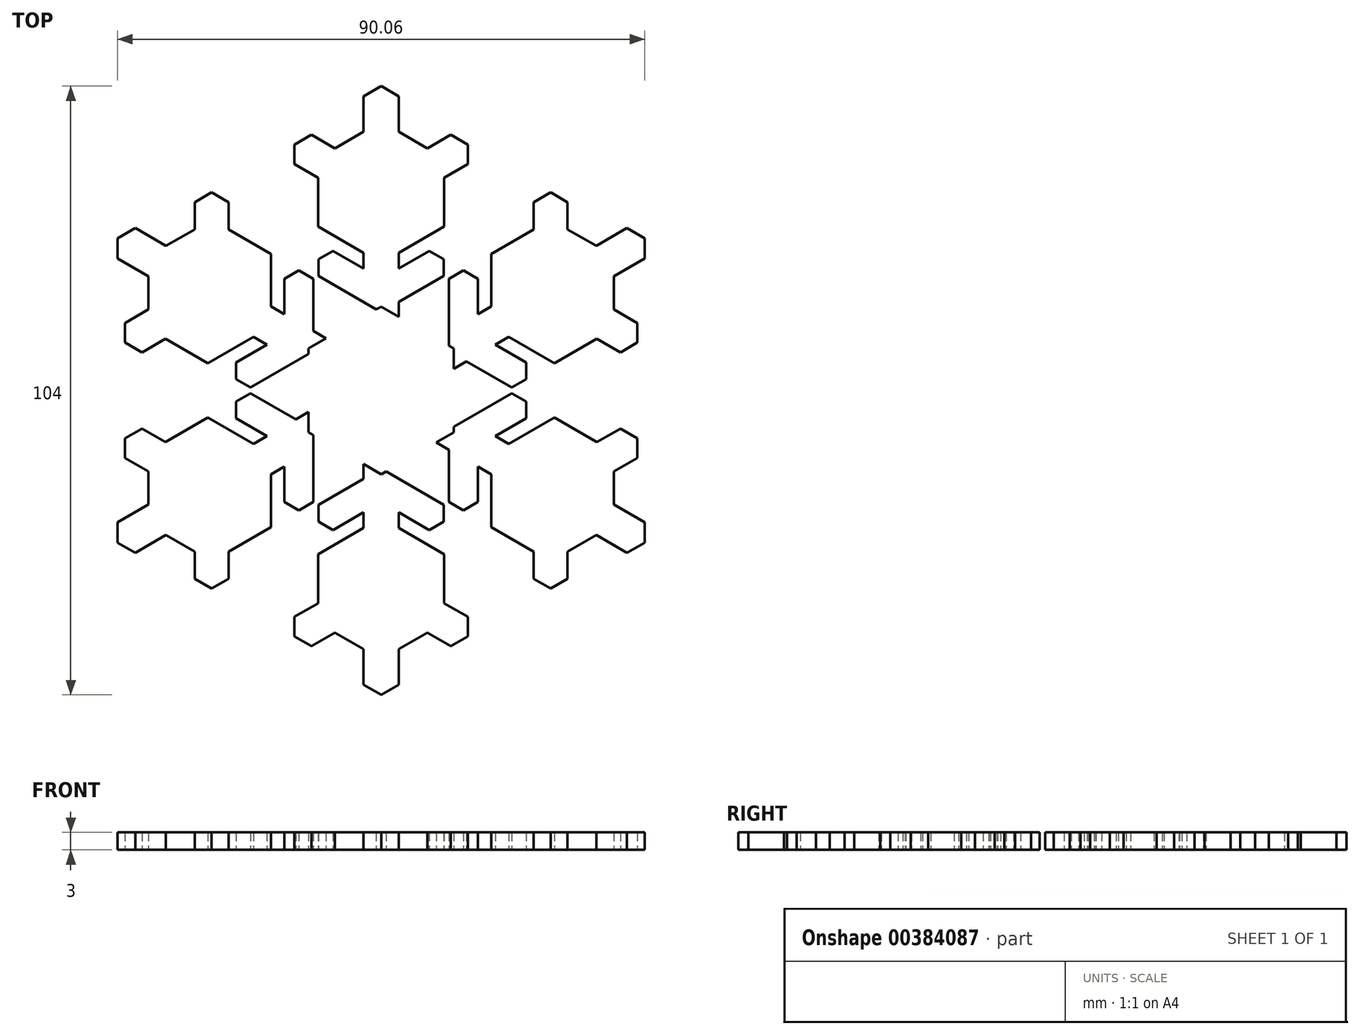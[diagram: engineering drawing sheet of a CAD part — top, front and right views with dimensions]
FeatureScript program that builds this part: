
annotation { "Feature Type Name" : "Feature", "Feature Type Description" : "" }
export const myFeature = defineFeature(function(context is Context, id is Id, definition is map)
    precondition{}
    {
        {
            var Q0;
            Q0=qCreatedBy(makeId("Top.planeOp"),FACE);
            var sketch = newSketch(context, id + "F0", { "sketchPlane" : qUnion([Q0])});
            skLineSegment(sketch, "E0", {"start": v(0, 26) * mm, "end": v(0, -26) * mm, "construction": true});
            skLineSegment(sketch, "E1", {"start": v(-22.52, -13) * mm, "end": v(22.52, 13) * mm, "construction": true});
            skLineSegment(sketch, "E2", {"start": v(22.52, -13) * mm, "end": v(-22.52, 13) * mm, "construction": true});
            skLineSegment(sketch, "E3", {"start": v(0, 7.16) * mm, "end": v(-6.2, 3.58) * mm});
            skLineSegment(sketch, "E4", {"start": v(-3.2, 1.85) * mm, "end": v(0, 3.7) * mm});
            skLineSegment(sketch, "E5", {"start": v(-1.5, 6.3) * mm, "end": v(-1.5, 11.75) * mm});
            skLineSegment(sketch, "E6", {"start": v(-1.5, 11.75) * mm, "end": v(-5.4, 14) * mm});
            skLineSegment(sketch, "E7", {"start": v(-5.4, 14) * mm, "end": v(-5.4, 19.85) * mm});
            skLineSegment(sketch, "E8", {"start": v(-5.4, 19.85) * mm, "end": v(-1.5, 22.1) * mm});
            skLineSegment(sketch, "E9", {"start": v(-1.5, 22.1) * mm, "end": v(-1.5, 25.13) * mm});
            skLineSegment(sketch, "E10", {"start": v(-1.5, 25.13) * mm, "end": v(0, 26) * mm});
            skLineSegment(sketch, "E11", {"start": v(-5.4, 18.18) * mm, "end": v(-7.4, 19.34) * mm});
            skLineSegment(sketch, "E12", {"start": v(-7.4, 19.34) * mm, "end": v(-7.4, 21) * mm});
            skLineSegment(sketch, "E13", {"start": v(-7.4, 21) * mm, "end": v(-5.95, 21.84) * mm});
            skLineSegment(sketch, "E14", {"start": v(-5.95, 21.84) * mm, "end": v(-3.95, 20.68) * mm});
            skLineSegment(sketch, "E15", {"start": v(-1.5, 22.1) * mm, "end": v(-1.5, 11.75) * mm, "construction": true});
            skLineSegment(sketch, "E16", {"start": v(-7.4, 19.34) * mm, "end": v(-5.95, 21.84) * mm, "construction": true});
            skLineSegment(sketch, "E17", {"start": v(-7.4, 21) * mm, "end": v(-6.68, 20.59) * mm, "construction": true});
            skLineSegment(sketch, "E18", {"start": v(-6.68, 20.59) * mm, "end": v(-5.4, 19.85) * mm, "construction": true});
            skLineSegment(sketch, "E19", {"start": v(-1.5, 10.4) * mm, "end": v(-4.12, 11.92) * mm});
            skLineSegment(sketch, "E20", {"start": v(-4.12, 11.92) * mm, "end": v(-5.36, 11.2) * mm});
            skLineSegment(sketch, "E21", {"start": v(-5.36, 11.2) * mm, "end": v(-5.36, 9.78) * mm});
            skLineSegment(sketch, "E22", {"start": v(-5.36, 9.78) * mm, "end": v(-0.42, 6.92) * mm});
            skLineSegment(sketch, "E23", {"start": v(-5.36, 9.78) * mm, "end": v(-4.12, 11.92) * mm, "construction": true});
            skPoint(sketch, "E24.endSnap0", {"position": v(-4.74, 10.85) * mm});
            skLineSegment(sketch, "E25", {"start": v(-5.36, 11.2) * mm, "end": v(-4.74, 10.85) * mm, "construction": true});
            skLineSegment(sketch, "E26.MirrorCS", {"start": v(7.4, 19.34) * mm, "end": v(5.95, 21.84) * mm, "construction": true});
            skLineSegment(sketch, "E27.MirrorCS", {"start": v(7.4, 19.34) * mm, "end": v(7.4, 21) * mm});
            skLineSegment(sketch, "E28.MirrorCS", {"start": v(6.68, 20.59) * mm, "end": v(5.4, 19.85) * mm, "construction": true});
            skLineSegment(sketch, "E29.MirrorCS", {"start": v(7.4, 21) * mm, "end": v(5.95, 21.84) * mm});
            skLineSegment(sketch, "E30.MirrorCS", {"start": v(7.4, 21) * mm, "end": v(6.68, 20.59) * mm, "construction": true});
            skLineSegment(sketch, "E31.MirrorCS", {"start": v(1.5, 25.13) * mm, "end": v(0, 26) * mm});
            skLineSegment(sketch, "E32.MirrorCS", {"start": v(5.36, 11.2) * mm, "end": v(4.74, 10.85) * mm, "construction": true});
            skLineSegment(sketch, "E33.MirrorCS", {"start": v(1.5, 22.1) * mm, "end": v(1.5, 25.13) * mm});
            skLineSegment(sketch, "E34.MirrorCS", {"start": v(5.4, 19.85) * mm, "end": v(1.5, 22.1) * mm});
            skLineSegment(sketch, "E35.MirrorCS", {"start": v(1.5, 10.4) * mm, "end": v(4.12, 11.92) * mm});
            skLineSegment(sketch, "E36.MirrorCS", {"start": v(4.12, 11.92) * mm, "end": v(5.36, 11.2) * mm});
            skLineSegment(sketch, "E37.MirrorCS", {"start": v(5.36, 9.78) * mm, "end": v(0.42, 6.92) * mm});
            skLineSegment(sketch, "E38.MirrorCS", {"start": v(5.36, 9.78) * mm, "end": v(4.12, 11.92) * mm, "construction": true});
            skLineSegment(sketch, "E39.MirrorCS", {"start": v(5.4, 18.18) * mm, "end": v(7.4, 19.34) * mm});
            skPoint(sketch, "E40.MirrorP", {"position": v(4.74, 10.85) * mm});
            skLineSegment(sketch, "E41.MirrorCS", {"start": v(3.2, 1.85) * mm, "end": v(0, 3.7) * mm});
            skLineSegment(sketch, "E42.MirrorCS", {"start": v(0, 7.16) * mm, "end": v(6.2, 3.58) * mm});
            skLineSegment(sketch, "E43.MirrorCS", {"start": v(1.5, 6.3) * mm, "end": v(1.5, 11.75) * mm});
            skLineSegment(sketch, "E44.MirrorCS", {"start": v(1.5, 11.75) * mm, "end": v(5.4, 14) * mm});
            skLineSegment(sketch, "E45.MirrorCS", {"start": v(5.36, 11.2) * mm, "end": v(5.36, 9.78) * mm});
            skLineSegment(sketch, "E46.MirrorCS", {"start": v(5.4, 14) * mm, "end": v(5.4, 19.85) * mm});
            skLineSegment(sketch, "E47.MirrorCS", {"start": v(1.5, 22.1) * mm, "end": v(1.5, 11.75) * mm, "construction": true});
            skLineSegment(sketch, "E48.MirrorCS", {"start": v(5.95, 21.84) * mm, "end": v(3.95, 20.68) * mm});
            skLineSegment(sketch, "E49.1.0", {"start": v(-8.26, 9.53) * mm, "end": v(-7.02, 10.25) * mm});
            skLineSegment(sketch, "E49.1.1", {"start": v(-12.39, 2.39) * mm, "end": v(-12.39, 0.96) * mm});
            skLineSegment(sketch, "E49.1.2", {"start": v(0, 3.7) * mm, "end": v(-3.2, 1.85) * mm});
            skLineSegment(sketch, "E49.1.3", {"start": v(-10.92, 4.57) * mm, "end": v(-14.82, 2.33) * mm});
            skLineSegment(sketch, "E49.1.4", {"start": v(-18.39, 12.35) * mm, "end": v(-9.42, 7.17) * mm, "construction": true});
            skLineSegment(sketch, "E49.1.5", {"start": v(-11.15, 0.24) * mm, "end": v(-12.39, 2.39) * mm, "construction": true});
            skLineSegment(sketch, "E49.1.6", {"start": v(-5.79, 9.53) * mm, "end": v(-5.79, 3.82) * mm});
            skLineSegment(sketch, "E49.1.7", {"start": v(-21.9, 5.76) * mm, "end": v(-19.89, 6.92) * mm});
            skLineSegment(sketch, "E49.1.8", {"start": v(-19.89, 9.75) * mm, "end": v(-10.92, 4.57) * mm, "construction": true});
            skLineSegment(sketch, "E49.1.9", {"start": v(-18.44, 4.42) * mm, "end": v(-20.45, 3.26) * mm});
            skLineSegment(sketch, "E49.1.10", {"start": v(-7.02, 10.25) * mm, "end": v(-5.79, 9.53) * mm});
            skLineSegment(sketch, "E49.1.11", {"start": v(-14.82, 2.33) * mm, "end": v(-19.89, 5.25) * mm});
            skLineSegment(sketch, "E49.1.12", {"start": v(-6.2, 1.85) * mm, "end": v(-10.92, 4.57) * mm});
            skLineSegment(sketch, "E49.1.13", {"start": v(-9.42, 7.17) * mm, "end": v(-9.42, 11.67) * mm});
            skLineSegment(sketch, "E49.1.14", {"start": v(-3.2, -1.85) * mm, "end": v(-3.2, 1.85) * mm});
            skLineSegment(sketch, "E49.1.15", {"start": v(-6.2, 3.58) * mm, "end": v(-6.2, -3.58) * mm});
            skLineSegment(sketch, "E49.1.16", {"start": v(-18.39, 12.35) * mm, "end": v(-21.02, 13.87) * mm});
            skPoint(sketch, "E49.1.17", {"position": v(-11.77, 1.32) * mm});
            skLineSegment(sketch, "E49.1.18", {"start": v(-9.42, 11.67) * mm, "end": v(-14.5, 14.6) * mm});
            skLineSegment(sketch, "E49.1.19", {"start": v(-6.2, 3.58) * mm, "end": v(0, 7.16) * mm});
            skLineSegment(sketch, "E49.1.20", {"start": v(-12.39, 0.96) * mm, "end": v(-11.15, 0.24) * mm});
            skLineSegment(sketch, "E49.1.21", {"start": v(-15.94, 16.08) * mm, "end": v(-15.94, 13.76) * mm});
            skLineSegment(sketch, "E49.1.22", {"start": v(-21.02, 13.87) * mm, "end": v(-22.52, 13) * mm});
            skLineSegment(sketch, "E49.1.23", {"start": v(-5.79, 9.53) * mm, "end": v(-8.26, 9.53) * mm, "construction": true});
            skPoint(sketch, "E49.1.24", {"position": v(-7.02, 9.53) * mm});
            skLineSegment(sketch, "E49.1.25", {"start": v(-4.7, 4.45) * mm, "end": v(-9.42, 7.17) * mm});
            skLineSegment(sketch, "E49.1.26", {"start": v(-11.15, 0.24) * mm, "end": v(-6.2, 3.1) * mm});
            skLineSegment(sketch, "E49.1.27", {"start": v(-13.05, 13.76) * mm, "end": v(-13.05, 16.08) * mm});
            skLineSegment(sketch, "E49.1.28", {"start": v(-8.26, 6.5) * mm, "end": v(-8.26, 9.53) * mm});
            skLineSegment(sketch, "E49.1.29", {"start": v(-9.76, 3.9) * mm, "end": v(-12.39, 2.39) * mm});
            skLineSegment(sketch, "E49.1.30", {"start": v(-19.89, 5.25) * mm, "end": v(-19.89, 9.75) * mm});
            skLineSegment(sketch, "E49.1.31", {"start": v(-19.89, 9.75) * mm, "end": v(-22.52, 11.27) * mm});
            skLineSegment(sketch, "E49.1.32", {"start": v(-14.5, 14.6) * mm, "end": v(-18.39, 12.35) * mm});
            skLineSegment(sketch, "E49.1.33", {"start": v(-14.5, 16.08) * mm, "end": v(-14.5, 14.6) * mm, "construction": true});
            skLineSegment(sketch, "E49.1.34", {"start": v(-14.5, 16.91) * mm, "end": v(-14.5, 16.08) * mm, "construction": true});
            skLineSegment(sketch, "E49.1.35", {"start": v(-22.52, 11.27) * mm, "end": v(-22.52, 13) * mm});
            skLineSegment(sketch, "E49.1.36", {"start": v(-12.39, 0.96) * mm, "end": v(-11.77, 1.32) * mm, "construction": true});
            skLineSegment(sketch, "E49.1.37", {"start": v(-13.05, 16.08) * mm, "end": v(-15.94, 16.08) * mm, "construction": true});
            skLineSegment(sketch, "E49.1.38", {"start": v(-7.02, 10.25) * mm, "end": v(-7.02, 9.53) * mm, "construction": true});
            skLineSegment(sketch, "E49.1.39", {"start": v(-21.9, 4.1) * mm, "end": v(-21.9, 5.76) * mm});
            skLineSegment(sketch, "E49.1.40", {"start": v(-20.45, 3.26) * mm, "end": v(-21.9, 4.1) * mm});
            skLineSegment(sketch, "E49.1.41", {"start": v(-13.05, 16.08) * mm, "end": v(-14.5, 16.91) * mm});
            skLineSegment(sketch, "E49.1.42", {"start": v(-20.45, 3.26) * mm, "end": v(-21.9, 5.76) * mm, "construction": true});
            skLineSegment(sketch, "E49.1.43", {"start": v(-14.5, 16.91) * mm, "end": v(-15.94, 16.08) * mm});
            skLineSegment(sketch, "E49.1.44", {"start": v(-21.9, 4.1) * mm, "end": v(-21.17, 4.51) * mm, "construction": true});
            skLineSegment(sketch, "E49.1.45", {"start": v(-21.17, 4.51) * mm, "end": v(-19.89, 5.25) * mm, "construction": true});
            skLineSegment(sketch, "E49.2.0", {"start": v(-12.39, -2.39) * mm, "end": v(-12.39, -0.96) * mm});
            skLineSegment(sketch, "E49.2.1", {"start": v(-8.26, -9.53) * mm, "end": v(-7.02, -10.25) * mm});
            skLineSegment(sketch, "E49.2.2", {"start": v(-3.2, 1.85) * mm, "end": v(-3.2, -1.85) * mm});
            skLineSegment(sketch, "E49.2.3", {"start": v(-9.42, -7.17) * mm, "end": v(-9.42, -11.67) * mm});
            skLineSegment(sketch, "E49.2.4", {"start": v(-19.89, -9.75) * mm, "end": v(-10.92, -4.57) * mm, "construction": true});
            skLineSegment(sketch, "E49.2.5", {"start": v(-5.79, -9.53) * mm, "end": v(-8.26, -9.53) * mm, "construction": true});
            skLineSegment(sketch, "E49.2.6", {"start": v(-11.15, -0.24) * mm, "end": v(-6.2, -3.1) * mm});
            skLineSegment(sketch, "E49.2.7", {"start": v(-15.94, -16.08) * mm, "end": v(-15.94, -13.76) * mm});
            skLineSegment(sketch, "E49.2.8", {"start": v(-18.39, -12.35) * mm, "end": v(-9.42, -7.17) * mm, "construction": true});
            skLineSegment(sketch, "E49.2.9", {"start": v(-13.05, -13.76) * mm, "end": v(-13.05, -16.08) * mm});
            skLineSegment(sketch, "E49.2.10", {"start": v(-12.39, -0.96) * mm, "end": v(-11.15, -0.24) * mm});
            skLineSegment(sketch, "E49.2.11", {"start": v(-9.42, -11.67) * mm, "end": v(-14.5, -14.6) * mm});
            skLineSegment(sketch, "E49.2.12", {"start": v(-4.7, -4.45) * mm, "end": v(-9.42, -7.17) * mm});
            skLineSegment(sketch, "E49.2.13", {"start": v(-10.92, -4.57) * mm, "end": v(-14.82, -2.33) * mm});
            skLineSegment(sketch, "E49.2.14", {"start": v(0, -3.7) * mm, "end": v(-3.2, -1.85) * mm});
            skLineSegment(sketch, "E49.2.15", {"start": v(-6.2, -3.58) * mm, "end": v(0, -7.16) * mm});
            skLineSegment(sketch, "E49.2.16", {"start": v(-19.89, -9.75) * mm, "end": v(-22.52, -11.27) * mm});
            skPoint(sketch, "E49.2.17", {"position": v(-7.02, -9.53) * mm});
            skLineSegment(sketch, "E49.2.18", {"start": v(-14.82, -2.33) * mm, "end": v(-19.89, -5.25) * mm});
            skLineSegment(sketch, "E49.2.19", {"start": v(-6.2, -3.58) * mm, "end": v(-6.2, 3.58) * mm});
            skLineSegment(sketch, "E49.2.20", {"start": v(-7.02, -10.25) * mm, "end": v(-5.79, -9.53) * mm});
            skLineSegment(sketch, "E49.2.21", {"start": v(-21.9, -5.76) * mm, "end": v(-19.89, -6.92) * mm});
            skLineSegment(sketch, "E49.2.22", {"start": v(-22.52, -11.27) * mm, "end": v(-22.52, -13) * mm});
            skLineSegment(sketch, "E49.2.23", {"start": v(-11.15, -0.24) * mm, "end": v(-12.39, -2.39) * mm, "construction": true});
            skPoint(sketch, "E49.2.24", {"position": v(-11.77, -1.32) * mm});
            skLineSegment(sketch, "E49.2.25", {"start": v(-6.2, -1.85) * mm, "end": v(-10.92, -4.57) * mm});
            skLineSegment(sketch, "E49.2.26", {"start": v(-5.79, -9.53) * mm, "end": v(-5.79, -3.82) * mm});
            skLineSegment(sketch, "E49.2.27", {"start": v(-18.44, -4.42) * mm, "end": v(-20.45, -3.26) * mm});
            skLineSegment(sketch, "E49.2.28", {"start": v(-9.76, -3.9) * mm, "end": v(-12.39, -2.39) * mm});
            skLineSegment(sketch, "E49.2.29", {"start": v(-8.26, -6.5) * mm, "end": v(-8.26, -9.53) * mm});
            skLineSegment(sketch, "E49.2.30", {"start": v(-14.5, -14.6) * mm, "end": v(-18.39, -12.35) * mm});
            skLineSegment(sketch, "E49.2.31", {"start": v(-18.39, -12.35) * mm, "end": v(-21.02, -13.87) * mm});
            skLineSegment(sketch, "E49.2.32", {"start": v(-19.89, -5.25) * mm, "end": v(-19.89, -9.75) * mm});
            skLineSegment(sketch, "E49.2.33", {"start": v(-21.17, -4.51) * mm, "end": v(-19.89, -5.25) * mm, "construction": true});
            skLineSegment(sketch, "E49.2.34", {"start": v(-21.9, -4.1) * mm, "end": v(-21.17, -4.51) * mm, "construction": true});
            skLineSegment(sketch, "E49.2.35", {"start": v(-21.02, -13.87) * mm, "end": v(-22.52, -13) * mm});
            skLineSegment(sketch, "E49.2.36", {"start": v(-7.02, -10.25) * mm, "end": v(-7.02, -9.53) * mm, "construction": true});
            skLineSegment(sketch, "E49.2.37", {"start": v(-20.45, -3.26) * mm, "end": v(-21.9, -5.76) * mm, "construction": true});
            skLineSegment(sketch, "E49.2.38", {"start": v(-12.39, -0.96) * mm, "end": v(-11.77, -1.32) * mm, "construction": true});
            skLineSegment(sketch, "E49.2.39", {"start": v(-14.5, -16.91) * mm, "end": v(-15.94, -16.08) * mm});
            skLineSegment(sketch, "E49.2.40", {"start": v(-13.05, -16.08) * mm, "end": v(-14.5, -16.91) * mm});
            skLineSegment(sketch, "E49.2.41", {"start": v(-20.45, -3.26) * mm, "end": v(-21.9, -4.1) * mm});
            skLineSegment(sketch, "E49.2.42", {"start": v(-13.05, -16.08) * mm, "end": v(-15.94, -16.08) * mm, "construction": true});
            skLineSegment(sketch, "E49.2.43", {"start": v(-21.9, -4.1) * mm, "end": v(-21.9, -5.76) * mm});
            skLineSegment(sketch, "E49.2.44", {"start": v(-14.5, -16.91) * mm, "end": v(-14.5, -16.08) * mm, "construction": true});
            skLineSegment(sketch, "E49.2.45", {"start": v(-14.5, -16.08) * mm, "end": v(-14.5, -14.6) * mm, "construction": true});
            skLineSegment(sketch, "E49.3.0", {"start": v(-4.12, -11.92) * mm, "end": v(-5.36, -11.2) * mm});
            skLineSegment(sketch, "E49.3.1", {"start": v(4.12, -11.92) * mm, "end": v(5.36, -11.2) * mm});
            skLineSegment(sketch, "E49.3.2", {"start": v(-3.2, -1.85) * mm, "end": v(0, -3.7) * mm});
            skLineSegment(sketch, "E49.3.3", {"start": v(1.5, -11.75) * mm, "end": v(5.4, -14) * mm});
            skLineSegment(sketch, "E49.3.4", {"start": v(-1.5, -22.1) * mm, "end": v(-1.5, -11.75) * mm, "construction": true});
            skLineSegment(sketch, "E49.3.5", {"start": v(5.36, -9.78) * mm, "end": v(4.12, -11.92) * mm, "construction": true});
            skLineSegment(sketch, "E49.3.6", {"start": v(-5.36, -9.78) * mm, "end": v(-0.42, -6.92) * mm});
            skLineSegment(sketch, "E49.3.7", {"start": v(5.95, -21.84) * mm, "end": v(3.95, -20.68) * mm});
            skLineSegment(sketch, "E49.3.8", {"start": v(1.5, -22.1) * mm, "end": v(1.5, -11.75) * mm, "construction": true});
            skLineSegment(sketch, "E49.3.9", {"start": v(5.4, -18.18) * mm, "end": v(7.4, -19.34) * mm});
            skLineSegment(sketch, "E49.3.10", {"start": v(-5.36, -11.2) * mm, "end": v(-5.36, -9.78) * mm});
            skLineSegment(sketch, "E49.3.11", {"start": v(5.4, -14) * mm, "end": v(5.4, -19.85) * mm});
            skLineSegment(sketch, "E49.3.12", {"start": v(1.5, -6.3) * mm, "end": v(1.5, -11.75) * mm});
            skLineSegment(sketch, "E49.3.13", {"start": v(-1.5, -11.75) * mm, "end": v(-5.4, -14) * mm});
            skLineSegment(sketch, "E49.3.14", {"start": v(3.2, -1.85) * mm, "end": v(0, -3.7) * mm});
            skLineSegment(sketch, "E49.3.15", {"start": v(0, -7.16) * mm, "end": v(6.2, -3.58) * mm});
            skLineSegment(sketch, "E49.3.16", {"start": v(-1.5, -22.1) * mm, "end": v(-1.5, -25.13) * mm});
            skPoint(sketch, "E49.3.17", {"position": v(4.74, -10.85) * mm});
            skLineSegment(sketch, "E49.3.18", {"start": v(-5.4, -14) * mm, "end": v(-5.4, -19.85) * mm});
            skLineSegment(sketch, "E49.3.19", {"start": v(0, -7.16) * mm, "end": v(-6.2, -3.58) * mm});
            skLineSegment(sketch, "E49.3.20", {"start": v(5.36, -11.2) * mm, "end": v(5.36, -9.78) * mm});
            skLineSegment(sketch, "E49.3.21", {"start": v(-5.95, -21.84) * mm, "end": v(-3.95, -20.68) * mm});
            skLineSegment(sketch, "E49.3.22", {"start": v(-1.5, -25.13) * mm, "end": v(0, -26) * mm});
            skLineSegment(sketch, "E49.3.23", {"start": v(-5.36, -9.78) * mm, "end": v(-4.12, -11.92) * mm, "construction": true});
            skPoint(sketch, "E49.3.24", {"position": v(-4.74, -10.85) * mm});
            skLineSegment(sketch, "E49.3.25", {"start": v(-1.5, -6.3) * mm, "end": v(-1.5, -11.75) * mm});
            skLineSegment(sketch, "E49.3.26", {"start": v(5.36, -9.78) * mm, "end": v(0.42, -6.92) * mm});
            skLineSegment(sketch, "E49.3.27", {"start": v(-5.4, -18.18) * mm, "end": v(-7.4, -19.34) * mm});
            skLineSegment(sketch, "E49.3.28", {"start": v(-1.5, -10.4) * mm, "end": v(-4.12, -11.92) * mm});
            skLineSegment(sketch, "E49.3.29", {"start": v(1.5, -10.4) * mm, "end": v(4.12, -11.92) * mm});
            skLineSegment(sketch, "E49.3.30", {"start": v(5.4, -19.85) * mm, "end": v(1.5, -22.1) * mm});
            skLineSegment(sketch, "E49.3.31", {"start": v(1.5, -22.1) * mm, "end": v(1.5, -25.13) * mm});
            skLineSegment(sketch, "E49.3.32", {"start": v(-5.4, -19.85) * mm, "end": v(-1.5, -22.1) * mm});
            skLineSegment(sketch, "E49.3.33", {"start": v(-6.68, -20.59) * mm, "end": v(-5.4, -19.85) * mm, "construction": true});
            skLineSegment(sketch, "E49.3.34", {"start": v(-7.4, -21) * mm, "end": v(-6.68, -20.59) * mm, "construction": true});
            skLineSegment(sketch, "E49.3.35", {"start": v(1.5, -25.13) * mm, "end": v(0, -26) * mm});
            skLineSegment(sketch, "E49.3.36", {"start": v(5.36, -11.2) * mm, "end": v(4.74, -10.85) * mm, "construction": true});
            skLineSegment(sketch, "E49.3.37", {"start": v(-7.4, -19.34) * mm, "end": v(-5.95, -21.84) * mm, "construction": true});
            skLineSegment(sketch, "E49.3.38", {"start": v(-5.36, -11.2) * mm, "end": v(-4.74, -10.85) * mm, "construction": true});
            skLineSegment(sketch, "E49.3.39", {"start": v(7.4, -21) * mm, "end": v(5.95, -21.84) * mm});
            skLineSegment(sketch, "E49.3.40", {"start": v(7.4, -19.34) * mm, "end": v(7.4, -21) * mm});
            skLineSegment(sketch, "E49.3.41", {"start": v(-7.4, -19.34) * mm, "end": v(-7.4, -21) * mm});
            skLineSegment(sketch, "E49.3.42", {"start": v(7.4, -19.34) * mm, "end": v(5.95, -21.84) * mm, "construction": true});
            skLineSegment(sketch, "E49.3.43", {"start": v(-7.4, -21) * mm, "end": v(-5.95, -21.84) * mm});
            skLineSegment(sketch, "E49.3.44", {"start": v(7.4, -21) * mm, "end": v(6.68, -20.59) * mm, "construction": true});
            skLineSegment(sketch, "E49.3.45", {"start": v(6.68, -20.59) * mm, "end": v(5.4, -19.85) * mm, "construction": true});
            skLineSegment(sketch, "E49.4.0", {"start": v(8.26, -9.53) * mm, "end": v(7.02, -10.25) * mm});
            skLineSegment(sketch, "E49.4.1", {"start": v(12.39, -2.39) * mm, "end": v(12.39, -0.96) * mm});
            skLineSegment(sketch, "E49.4.2", {"start": v(0, -3.7) * mm, "end": v(3.2, -1.85) * mm});
            skLineSegment(sketch, "E49.4.3", {"start": v(10.92, -4.57) * mm, "end": v(14.82, -2.33) * mm});
            skLineSegment(sketch, "E49.4.4", {"start": v(18.39, -12.35) * mm, "end": v(9.42, -7.17) * mm, "construction": true});
            skLineSegment(sketch, "E49.4.5", {"start": v(11.15, -0.24) * mm, "end": v(12.39, -2.39) * mm, "construction": true});
            skLineSegment(sketch, "E49.4.6", {"start": v(5.79, -9.53) * mm, "end": v(5.79, -3.82) * mm});
            skLineSegment(sketch, "E49.4.7", {"start": v(21.9, -5.76) * mm, "end": v(19.89, -6.92) * mm});
            skLineSegment(sketch, "E49.4.8", {"start": v(19.89, -9.75) * mm, "end": v(10.92, -4.57) * mm, "construction": true});
            skLineSegment(sketch, "E49.4.9", {"start": v(18.44, -4.42) * mm, "end": v(20.45, -3.26) * mm});
            skLineSegment(sketch, "E49.4.10", {"start": v(7.02, -10.25) * mm, "end": v(5.79, -9.53) * mm});
            skLineSegment(sketch, "E49.4.11", {"start": v(14.82, -2.33) * mm, "end": v(19.89, -5.25) * mm});
            skLineSegment(sketch, "E49.4.12", {"start": v(6.2, -1.85) * mm, "end": v(10.92, -4.57) * mm});
            skLineSegment(sketch, "E49.4.13", {"start": v(9.42, -7.17) * mm, "end": v(9.42, -11.67) * mm});
            skLineSegment(sketch, "E49.4.14", {"start": v(3.2, 1.85) * mm, "end": v(3.2, -1.85) * mm});
            skLineSegment(sketch, "E49.4.15", {"start": v(6.2, -3.58) * mm, "end": v(6.2, 3.58) * mm});
            skLineSegment(sketch, "E49.4.16", {"start": v(18.39, -12.35) * mm, "end": v(21.02, -13.87) * mm});
            skPoint(sketch, "E49.4.17", {"position": v(11.77, -1.32) * mm});
            skLineSegment(sketch, "E49.4.18", {"start": v(9.42, -11.67) * mm, "end": v(14.5, -14.6) * mm});
            skLineSegment(sketch, "E49.4.19", {"start": v(6.2, -3.58) * mm, "end": v(0, -7.16) * mm});
            skLineSegment(sketch, "E49.4.20", {"start": v(12.39, -0.96) * mm, "end": v(11.15, -0.24) * mm});
            skLineSegment(sketch, "E49.4.21", {"start": v(15.94, -16.08) * mm, "end": v(15.94, -13.76) * mm});
            skLineSegment(sketch, "E49.4.22", {"start": v(21.02, -13.87) * mm, "end": v(22.52, -13) * mm});
            skLineSegment(sketch, "E49.4.23", {"start": v(5.79, -9.53) * mm, "end": v(8.26, -9.53) * mm, "construction": true});
            skPoint(sketch, "E49.4.24", {"position": v(7.02, -9.53) * mm});
            skLineSegment(sketch, "E49.4.25", {"start": v(4.7, -4.45) * mm, "end": v(9.42, -7.17) * mm});
            skLineSegment(sketch, "E49.4.26", {"start": v(11.15, -0.24) * mm, "end": v(6.2, -3.1) * mm});
            skLineSegment(sketch, "E49.4.27", {"start": v(13.05, -13.76) * mm, "end": v(13.05, -16.08) * mm});
            skLineSegment(sketch, "E49.4.28", {"start": v(8.26, -6.5) * mm, "end": v(8.26, -9.53) * mm});
            skLineSegment(sketch, "E49.4.29", {"start": v(9.76, -3.9) * mm, "end": v(12.39, -2.39) * mm});
            skLineSegment(sketch, "E49.4.30", {"start": v(19.89, -5.25) * mm, "end": v(19.89, -9.75) * mm});
            skLineSegment(sketch, "E49.4.31", {"start": v(19.89, -9.75) * mm, "end": v(22.52, -11.27) * mm});
            skLineSegment(sketch, "E49.4.32", {"start": v(14.5, -14.6) * mm, "end": v(18.39, -12.35) * mm});
            skLineSegment(sketch, "E49.4.33", {"start": v(14.5, -16.08) * mm, "end": v(14.5, -14.6) * mm, "construction": true});
            skLineSegment(sketch, "E49.4.34", {"start": v(14.5, -16.91) * mm, "end": v(14.5, -16.08) * mm, "construction": true});
            skLineSegment(sketch, "E49.4.35", {"start": v(22.52, -11.27) * mm, "end": v(22.52, -13) * mm});
            skLineSegment(sketch, "E49.4.36", {"start": v(12.39, -0.96) * mm, "end": v(11.77, -1.32) * mm, "construction": true});
            skLineSegment(sketch, "E49.4.37", {"start": v(13.05, -16.08) * mm, "end": v(15.94, -16.08) * mm, "construction": true});
            skLineSegment(sketch, "E49.4.38", {"start": v(7.02, -10.25) * mm, "end": v(7.02, -9.53) * mm, "construction": true});
            skLineSegment(sketch, "E49.4.39", {"start": v(21.9, -4.1) * mm, "end": v(21.9, -5.76) * mm});
            skLineSegment(sketch, "E49.4.40", {"start": v(20.45, -3.26) * mm, "end": v(21.9, -4.1) * mm});
            skLineSegment(sketch, "E49.4.41", {"start": v(13.05, -16.08) * mm, "end": v(14.5, -16.91) * mm});
            skLineSegment(sketch, "E49.4.42", {"start": v(20.45, -3.26) * mm, "end": v(21.9, -5.76) * mm, "construction": true});
            skLineSegment(sketch, "E49.4.43", {"start": v(14.5, -16.91) * mm, "end": v(15.94, -16.08) * mm});
            skLineSegment(sketch, "E49.4.44", {"start": v(21.9, -4.1) * mm, "end": v(21.17, -4.51) * mm, "construction": true});
            skLineSegment(sketch, "E49.4.45", {"start": v(21.17, -4.51) * mm, "end": v(19.89, -5.25) * mm, "construction": true});
            skLineSegment(sketch, "E49.5.0", {"start": v(12.39, 2.39) * mm, "end": v(12.39, 0.96) * mm});
            skLineSegment(sketch, "E49.5.1", {"start": v(8.26, 9.53) * mm, "end": v(7.02, 10.25) * mm});
            skLineSegment(sketch, "E49.5.2", {"start": v(3.2, -1.85) * mm, "end": v(3.2, 1.85) * mm});
            skLineSegment(sketch, "E49.5.3", {"start": v(9.42, 7.17) * mm, "end": v(9.42, 11.67) * mm});
            skLineSegment(sketch, "E49.5.4", {"start": v(19.89, 9.75) * mm, "end": v(10.92, 4.57) * mm, "construction": true});
            skLineSegment(sketch, "E49.5.5", {"start": v(5.79, 9.53) * mm, "end": v(8.26, 9.53) * mm, "construction": true});
            skLineSegment(sketch, "E49.5.6", {"start": v(11.15, 0.24) * mm, "end": v(6.2, 3.1) * mm});
            skLineSegment(sketch, "E49.5.7", {"start": v(15.94, 16.08) * mm, "end": v(15.94, 13.76) * mm});
            skLineSegment(sketch, "E49.5.8", {"start": v(18.39, 12.35) * mm, "end": v(9.42, 7.17) * mm, "construction": true});
            skLineSegment(sketch, "E49.5.9", {"start": v(13.05, 13.76) * mm, "end": v(13.05, 16.08) * mm});
            skLineSegment(sketch, "E49.5.10", {"start": v(12.39, 0.96) * mm, "end": v(11.15, 0.24) * mm});
            skLineSegment(sketch, "E49.5.11", {"start": v(9.42, 11.67) * mm, "end": v(14.5, 14.6) * mm});
            skLineSegment(sketch, "E49.5.12", {"start": v(4.7, 4.45) * mm, "end": v(9.42, 7.17) * mm});
            skLineSegment(sketch, "E49.5.13", {"start": v(10.92, 4.57) * mm, "end": v(14.82, 2.33) * mm});
            skLineSegment(sketch, "E49.5.14", {"start": v(0, 3.7) * mm, "end": v(3.2, 1.85) * mm});
            skLineSegment(sketch, "E49.5.15", {"start": v(6.2, 3.58) * mm, "end": v(0, 7.16) * mm});
            skLineSegment(sketch, "E49.5.16", {"start": v(19.89, 9.75) * mm, "end": v(22.52, 11.27) * mm});
            skPoint(sketch, "E49.5.17", {"position": v(7.02, 9.53) * mm});
            skLineSegment(sketch, "E49.5.18", {"start": v(14.82, 2.33) * mm, "end": v(19.89, 5.25) * mm});
            skLineSegment(sketch, "E49.5.19", {"start": v(6.2, 3.58) * mm, "end": v(6.2, -3.58) * mm});
            skLineSegment(sketch, "E49.5.20", {"start": v(7.02, 10.25) * mm, "end": v(5.79, 9.53) * mm});
            skLineSegment(sketch, "E49.5.21", {"start": v(21.9, 5.76) * mm, "end": v(19.89, 6.92) * mm});
            skLineSegment(sketch, "E49.5.22", {"start": v(22.52, 11.27) * mm, "end": v(22.52, 13) * mm});
            skLineSegment(sketch, "E49.5.23", {"start": v(11.15, 0.24) * mm, "end": v(12.39, 2.39) * mm, "construction": true});
            skPoint(sketch, "E49.5.24", {"position": v(11.77, 1.32) * mm});
            skLineSegment(sketch, "E49.5.25", {"start": v(6.2, 1.85) * mm, "end": v(10.92, 4.57) * mm});
            skLineSegment(sketch, "E49.5.26", {"start": v(5.79, 9.53) * mm, "end": v(5.79, 3.82) * mm});
            skLineSegment(sketch, "E49.5.27", {"start": v(18.44, 4.42) * mm, "end": v(20.45, 3.26) * mm});
            skLineSegment(sketch, "E49.5.28", {"start": v(9.76, 3.9) * mm, "end": v(12.39, 2.39) * mm});
            skLineSegment(sketch, "E49.5.29", {"start": v(8.26, 6.5) * mm, "end": v(8.26, 9.53) * mm});
            skLineSegment(sketch, "E49.5.30", {"start": v(14.5, 14.6) * mm, "end": v(18.39, 12.35) * mm});
            skLineSegment(sketch, "E49.5.31", {"start": v(18.39, 12.35) * mm, "end": v(21.02, 13.87) * mm});
            skLineSegment(sketch, "E49.5.32", {"start": v(19.89, 5.25) * mm, "end": v(19.89, 9.75) * mm});
            skLineSegment(sketch, "E49.5.33", {"start": v(21.17, 4.51) * mm, "end": v(19.89, 5.25) * mm, "construction": true});
            skLineSegment(sketch, "E49.5.34", {"start": v(21.9, 4.1) * mm, "end": v(21.17, 4.51) * mm, "construction": true});
            skLineSegment(sketch, "E49.5.35", {"start": v(21.02, 13.87) * mm, "end": v(22.52, 13) * mm});
            skLineSegment(sketch, "E49.5.36", {"start": v(7.02, 10.25) * mm, "end": v(7.02, 9.53) * mm, "construction": true});
            skLineSegment(sketch, "E49.5.37", {"start": v(20.45, 3.26) * mm, "end": v(21.9, 5.76) * mm, "construction": true});
            skLineSegment(sketch, "E49.5.38", {"start": v(12.39, 0.96) * mm, "end": v(11.77, 1.32) * mm, "construction": true});
            skLineSegment(sketch, "E49.5.39", {"start": v(14.5, 16.91) * mm, "end": v(15.94, 16.08) * mm});
            skLineSegment(sketch, "E49.5.40", {"start": v(13.05, 16.08) * mm, "end": v(14.5, 16.91) * mm});
            skLineSegment(sketch, "E49.5.41", {"start": v(20.45, 3.26) * mm, "end": v(21.9, 4.1) * mm});
            skLineSegment(sketch, "E49.5.42", {"start": v(13.05, 16.08) * mm, "end": v(15.94, 16.08) * mm, "construction": true});
            skLineSegment(sketch, "E49.5.43", {"start": v(21.9, 4.1) * mm, "end": v(21.9, 5.76) * mm});
            skLineSegment(sketch, "E49.5.44", {"start": v(14.5, 16.91) * mm, "end": v(14.5, 16.08) * mm, "construction": true});
            skLineSegment(sketch, "E49.5.45", {"start": v(14.5, 16.08) * mm, "end": v(14.5, 14.6) * mm, "construction": true});
            skPoint(sketch, "E49.center", {"position": v(0, 0) * mm});
            skSolve(sketch);
        }
        {
            var Q0;
            Q0=makeQuery(id+"F0.imprint","IMPRINT",FACE,{"disambiguationData":[TD([[makeQuery(id+"F0.imprint","IMPRINT",EDGE,{"derivedFrom":sQuery(id+"F0.wireOp",EDGE,"E49.1.0")}),-1.0]])]});
            var Q1;
            Q1=makeQuery(id+"F0.imprint","IMPRINT",FACE,{"disambiguationData":[TD([[makeQuery(id+"F0.imprint","IMPRINT",EDGE,{"derivedFrom":sQuery(id+"F0.wireOp",EDGE,"E49.5.1")}),1.0]])]});
            var Q2;
            Q2=makeQuery(id+"F0.imprint","IMPRINT",FACE,{"disambiguationData":[TD([[makeQuery(id+"F0.imprint","IMPRINT",EDGE,{"derivedFrom":sQuery(id+"F0.wireOp",EDGE,"E49.3.1")}),1.0]])]});
            var Q3;
            {var subQ7=sQuery(id+"F0.wireOp",EDGE,"E49.1.3");Q3=makeQuery(id+"F0.imprint","IMPRINT",FACE,{"disambiguationData":[TD([[makeQuery(id+"F0.imprint","IMPRINT",EDGE,{"derivedFrom":subQ7}),-1.0]])]});}
            var Q4;
            {var subQ7=sQuery(id+"F0.wireOp",EDGE,"E49.4.3");Q4=makeQuery(id+"F0.imprint","IMPRINT",FACE,{"disambiguationData":[TD([[makeQuery(id+"F0.imprint","IMPRINT",EDGE,{"derivedFrom":subQ7}),-1.0]])]});}
            var Q5;
            {var subQ0=sQuery(id+"F0.wireOp",EDGE,"E19");Q5=makeQuery(id+"F0.imprint","IMPRINT",FACE,{"disambiguationData":[TD([[makeQuery(id+"F0.imprint","IMPRINT",EDGE,{"derivedFrom":subQ0}),1.0]])]});}
            var Q6;
            {var subQ7=sQuery(id+"F0.wireOp",EDGE,"E49.3.3");Q6=makeQuery(id+"F0.imprint","IMPRINT",FACE,{"disambiguationData":[TD([[makeQuery(id+"F0.imprint","IMPRINT",EDGE,{"derivedFrom":subQ7}),-1.0]])]});}
            var Q7;
            {var subQ1=sQuery(id+"F0.wireOp",EDGE,"E49.5.7");Q7=makeQuery(id+"F0.imprint","IMPRINT",FACE,{"disambiguationData":[TD([[makeQuery(id+"F0.imprint","IMPRINT",EDGE,{"derivedFrom":subQ1}),-1.0]])]});}
            var Q8;
            Q8=makeQuery(id+"F0.imprint","IMPRINT",FACE,{"disambiguationData":[TD([[makeQuery(id+"F0.imprint","IMPRINT",EDGE,{"derivedFrom":sQuery(id+"F0.wireOp",EDGE,"E49.1.1")}),1.0]])]});
            var Q9;
            {var subQ1=sQuery(id+"F0.wireOp",EDGE,"E49.1.21");Q9=makeQuery(id+"F0.imprint","IMPRINT",FACE,{"disambiguationData":[TD([[makeQuery(id+"F0.imprint","IMPRINT",EDGE,{"derivedFrom":subQ1}),1.0]])]});}
            var Q10;
            {var subQ4=sQuery(id+"F0.wireOp",EDGE,"E35.MirrorCS");Q10=makeQuery(id+"F0.imprint","IMPRINT",FACE,{"disambiguationData":[TD([[makeQuery(id+"F0.imprint","IMPRINT",EDGE,{"derivedFrom":subQ4}),-1.0]])]});}
            var Q11;
            {var subQ7=sQuery(id+"F0.wireOp",EDGE,"E49.2.3");Q11=makeQuery(id+"F0.imprint","IMPRINT",FACE,{"disambiguationData":[TD([[makeQuery(id+"F0.imprint","IMPRINT",EDGE,{"derivedFrom":subQ7}),-1.0]])]});}
            var Q12;
            {var subQ1=sQuery(id+"F0.wireOp",EDGE,"E49.2.7");Q12=makeQuery(id+"F0.imprint","IMPRINT",FACE,{"disambiguationData":[TD([[makeQuery(id+"F0.imprint","IMPRINT",EDGE,{"derivedFrom":subQ1}),-1.0]])]});}
            var Q13;
            Q13=makeQuery(id+"F0.imprint","IMPRINT",FACE,{"disambiguationData":[TD([[makeQuery(id+"F0.imprint","IMPRINT",EDGE,{"derivedFrom":sQuery(id+"F0.wireOp",EDGE,"E49.2.1")}),1.0]])]});
            var Q14;
            Q14=makeQuery(id+"F0.imprint","IMPRINT",FACE,{"disambiguationData":[TD([[makeQuery(id+"F0.imprint","IMPRINT",EDGE,{"derivedFrom":sQuery(id+"F0.wireOp",EDGE,"E49.2.0")}),-1.0]])]});
            var Q15;
            Q15=makeQuery(id+"F0.imprint","IMPRINT",FACE,{"disambiguationData":[TD([[makeQuery(id+"F0.imprint","IMPRINT",EDGE,{"derivedFrom":sQuery(id+"F0.wireOp",EDGE,"E49.5.0")}),-1.0]])]});
            var Q16;
            {var subQ22=sQuery(id+"F0.wireOp",EDGE,"E6");Q16=makeQuery(id+"F0.imprint","IMPRINT",FACE,{"disambiguationData":[TD([[makeQuery(id+"F0.imprint","IMPRINT",EDGE,{"derivedFrom":subQ22}),-1.0]])]});}
            var Q17;
            Q17=makeQuery(id+"F0.imprint","IMPRINT",FACE,{"disambiguationData":[TD([[makeQuery(id+"F0.imprint","IMPRINT",EDGE,{"derivedFrom":sQuery(id+"F0.wireOp",EDGE,"E49.3.0")}),-1.0]])]});
            var Q18;
            {var subQ1=sQuery(id+"F0.wireOp",EDGE,"E49.4.21");Q18=makeQuery(id+"F0.imprint","IMPRINT",FACE,{"disambiguationData":[TD([[makeQuery(id+"F0.imprint","IMPRINT",EDGE,{"derivedFrom":subQ1}),1.0]])]});}
            var Q19;
            Q19=makeQuery(id+"F0.imprint","IMPRINT",FACE,{"disambiguationData":[TD([[makeQuery(id+"F0.imprint","IMPRINT",EDGE,{"derivedFrom":sQuery(id+"F0.wireOp",EDGE,"E49.4.1")}),1.0]])]});
            var Q20;
            Q20=makeQuery(id+"F0.imprint","IMPRINT",FACE,{"disambiguationData":[TD([[makeQuery(id+"F0.imprint","IMPRINT",EDGE,{"derivedFrom":sQuery(id+"F0.wireOp",EDGE,"E49.4.0")}),-1.0]])]});
            var Q21;
            Q21=makeQuery(id+"F0.imprint","IMPRINT",FACE,{"disambiguationData":[TD([[makeQuery(id+"F0.imprint","IMPRINT",EDGE,{"derivedFrom":sQuery(id+"F0.wireOp",EDGE,"E49.1.2")}),-1.0]])]});
            var Q22;
            {var subQ4=sQuery(id+"F0.wireOp",EDGE,"E49.5.3");Q22=makeQuery(id+"F0.imprint","IMPRINT",FACE,{"disambiguationData":[TD([[makeQuery(id+"F0.imprint","IMPRINT",EDGE,{"derivedFrom":subQ4}),-1.0]])]});}
            var Q23;
            {var subQ1=sQuery(id+"F0.wireOp",EDGE,"E49.5.21");Q23=makeQuery(id+"F0.imprint","IMPRINT",FACE,{"disambiguationData":[TD([[makeQuery(id+"F0.imprint","IMPRINT",EDGE,{"derivedFrom":subQ1}),1.0]])]});}
            var Q24;
            {var subQ1=sQuery(id+"F0.wireOp",EDGE,"E49.1.7");Q24=makeQuery(id+"F0.imprint","IMPRINT",FACE,{"disambiguationData":[TD([[makeQuery(id+"F0.imprint","IMPRINT",EDGE,{"derivedFrom":subQ1}),-1.0]])]});}
            var Q25;
            {var subQ1=sQuery(id+"F0.wireOp",EDGE,"E49.2.21");Q25=makeQuery(id+"F0.imprint","IMPRINT",FACE,{"disambiguationData":[TD([[makeQuery(id+"F0.imprint","IMPRINT",EDGE,{"derivedFrom":subQ1}),1.0]])]});}
            var Q26;
            Q26=makeQuery(id+"F0.imprint","IMPRINT",FACE,{"disambiguationData":[TD([[makeQuery(id+"F0.imprint","IMPRINT",EDGE,{"derivedFrom":sQuery(id+"F0.wireOp",EDGE,"E27.MirrorCS")}),1.0]])]});
            var Q27;
            {var subQ4=sQuery(id+"F0.wireOp",EDGE,"E11");Q27=makeQuery(id+"F0.imprint","IMPRINT",FACE,{"disambiguationData":[TD([[makeQuery(id+"F0.imprint","IMPRINT",EDGE,{"derivedFrom":subQ4}),-1.0]])]});}
            var Q28;
            {var subQ1=sQuery(id+"F0.wireOp",EDGE,"E49.3.7");Q28=makeQuery(id+"F0.imprint","IMPRINT",FACE,{"disambiguationData":[TD([[makeQuery(id+"F0.imprint","IMPRINT",EDGE,{"derivedFrom":subQ1}),-1.0]])]});}
            var Q29;
            {var subQ1=sQuery(id+"F0.wireOp",EDGE,"E49.4.7");Q29=makeQuery(id+"F0.imprint","IMPRINT",FACE,{"disambiguationData":[TD([[makeQuery(id+"F0.imprint","IMPRINT",EDGE,{"derivedFrom":subQ1}),-1.0]])]});}
            var Q30;
            {var subQ1=sQuery(id+"F0.wireOp",EDGE,"E49.3.21");Q30=makeQuery(id+"F0.imprint","IMPRINT",FACE,{"disambiguationData":[TD([[makeQuery(id+"F0.imprint","IMPRINT",EDGE,{"derivedFrom":subQ1}),1.0]])]});}
            var Q31;
            {var subQ0=sQuery(id+"F0.wireOp",EDGE,"E49.1.19");var subQ1=sQuery(id+"F0.wireOp",EDGE,"E5");var subQ2=makeQuery(id+"F0.imprint","INTERSECT",VERTEX,{"derivedFrom":[subQ1,subQ0]});Q31=makeQuery(id+"F0.imprint","IMPRINT",FACE,{"disambiguationData":[TD([[makeQuery(id+"F0.imprint","IMPRINT",EDGE,{"disambiguationData":[TD([[subQ2,-1.0]])],"derivedFrom":subQ1}),-1.0]])]});}
            var Q32;
            {var subQ0=sQuery(id+"F0.wireOp",EDGE,"E49.5.15");var subQ1=sQuery(id+"F0.wireOp",EDGE,"E49.5.12");var subQ2=makeQuery(id+"F0.imprint","INTERSECT",VERTEX,{"derivedFrom":[subQ1,subQ0]});Q32=makeQuery(id+"F0.imprint","IMPRINT",FACE,{"disambiguationData":[TD([[makeQuery(id+"F0.imprint","IMPRINT",EDGE,{"disambiguationData":[TD([[subQ2,-1.0]])],"derivedFrom":subQ1}),-1.0]])]});}
            var Q33;
            {var subQ0=sQuery(id+"F0.wireOp",EDGE,"E49.5.19");var subQ1=sQuery(id+"F0.wireOp",EDGE,"E49.5.6");var subQ2=makeQuery(id+"F0.imprint","INTERSECT",VERTEX,{"derivedFrom":[subQ1,subQ0]});Q33=makeQuery(id+"F0.imprint","IMPRINT",FACE,{"disambiguationData":[TD([[makeQuery(id+"F0.imprint","IMPRINT",EDGE,{"disambiguationData":[TD([[subQ2,1.0]])],"derivedFrom":subQ1}),1.0]])]});}
            var Q34;
            {var subQ0=sQuery(id+"F0.wireOp",EDGE,"E49.5.19");var subQ1=sQuery(id+"F0.wireOp",EDGE,"E49.4.12");var subQ2=makeQuery(id+"F0.imprint","INTERSECT",VERTEX,{"derivedFrom":[subQ1,subQ0]});Q34=makeQuery(id+"F0.imprint","IMPRINT",FACE,{"disambiguationData":[TD([[makeQuery(id+"F0.imprint","IMPRINT",EDGE,{"disambiguationData":[TD([[subQ2,-1.0]])],"derivedFrom":subQ1}),-1.0]])]});}
            var Q35;
            {var subQ0=sQuery(id+"F0.wireOp",EDGE,"E49.4.19");var subQ1=sQuery(id+"F0.wireOp",EDGE,"E49.4.6");var subQ2=makeQuery(id+"F0.imprint","INTERSECT",VERTEX,{"derivedFrom":[subQ1,subQ0]});Q35=makeQuery(id+"F0.imprint","IMPRINT",FACE,{"disambiguationData":[TD([[makeQuery(id+"F0.imprint","IMPRINT",EDGE,{"disambiguationData":[TD([[subQ2,1.0]])],"derivedFrom":subQ1}),1.0]])]});}
            var Q36;
            {var subQ0=sQuery(id+"F0.wireOp",EDGE,"E49.4.19");var subQ1=sQuery(id+"F0.wireOp",EDGE,"E49.3.12");var subQ2=makeQuery(id+"F0.imprint","INTERSECT",VERTEX,{"derivedFrom":[subQ1,subQ0]});Q36=makeQuery(id+"F0.imprint","IMPRINT",FACE,{"disambiguationData":[TD([[makeQuery(id+"F0.imprint","IMPRINT",EDGE,{"disambiguationData":[TD([[subQ2,-1.0]])],"derivedFrom":subQ1}),-1.0]])]});}
            var Q37;
            {var subQ0=sQuery(id+"F0.wireOp",EDGE,"E49.3.19");var subQ1=sQuery(id+"F0.wireOp",EDGE,"E49.2.12");var subQ2=makeQuery(id+"F0.imprint","INTERSECT",VERTEX,{"derivedFrom":[subQ1,subQ0]});Q37=makeQuery(id+"F0.imprint","IMPRINT",FACE,{"disambiguationData":[TD([[makeQuery(id+"F0.imprint","IMPRINT",EDGE,{"disambiguationData":[TD([[subQ2,-1.0]])],"derivedFrom":subQ1}),-1.0]])]});}
            var Q38;
            {var subQ0=sQuery(id+"F0.wireOp",EDGE,"E49.2.19");var subQ1=sQuery(id+"F0.wireOp",EDGE,"E49.2.6");var subQ2=makeQuery(id+"F0.imprint","INTERSECT",VERTEX,{"derivedFrom":[subQ1,subQ0]});Q38=makeQuery(id+"F0.imprint","IMPRINT",FACE,{"disambiguationData":[TD([[makeQuery(id+"F0.imprint","IMPRINT",EDGE,{"disambiguationData":[TD([[subQ2,1.0]])],"derivedFrom":subQ1}),1.0]])]});}
            var Q39;
            {var subQ0=sQuery(id+"F0.wireOp",EDGE,"E49.3.19");var subQ1=sQuery(id+"F0.wireOp",EDGE,"E49.3.6");var subQ2=makeQuery(id+"F0.imprint","INTERSECT",VERTEX,{"derivedFrom":[subQ1,subQ0]});Q39=makeQuery(id+"F0.imprint","IMPRINT",FACE,{"disambiguationData":[TD([[makeQuery(id+"F0.imprint","IMPRINT",EDGE,{"disambiguationData":[TD([[subQ2,1.0]])],"derivedFrom":subQ1}),1.0]])]});}
            var Q40;
            {var subQ0=sQuery(id+"F0.wireOp",EDGE,"E49.2.19");var subQ1=sQuery(id+"F0.wireOp",EDGE,"E49.1.12");var subQ2=makeQuery(id+"F0.imprint","INTERSECT",VERTEX,{"derivedFrom":[subQ1,subQ0]});Q40=makeQuery(id+"F0.imprint","IMPRINT",FACE,{"disambiguationData":[TD([[makeQuery(id+"F0.imprint","IMPRINT",EDGE,{"disambiguationData":[TD([[subQ2,-1.0]])],"derivedFrom":subQ1}),-1.0]])]});}
            var Q41;
            {var subQ0=sQuery(id+"F0.wireOp",EDGE,"E49.1.19");var subQ1=sQuery(id+"F0.wireOp",EDGE,"E49.1.6");var subQ2=makeQuery(id+"F0.imprint","INTERSECT",VERTEX,{"derivedFrom":[subQ1,subQ0]});Q41=makeQuery(id+"F0.imprint","IMPRINT",FACE,{"disambiguationData":[TD([[makeQuery(id+"F0.imprint","IMPRINT",EDGE,{"disambiguationData":[TD([[subQ2,1.0]])],"derivedFrom":subQ1}),1.0]])]});}
            var Q42;
            {var subQ0=sQuery(id+"F0.wireOp",EDGE,"E49.5.15");var subQ1=sQuery(id+"F0.wireOp",EDGE,"E37.MirrorCS");var subQ2=makeQuery(id+"F0.imprint","INTERSECT",VERTEX,{"derivedFrom":[subQ1,subQ0]});Q42=makeQuery(id+"F0.imprint","IMPRINT",FACE,{"disambiguationData":[TD([[makeQuery(id+"F0.imprint","IMPRINT",EDGE,{"disambiguationData":[TD([[subQ2,1.0]])],"derivedFrom":subQ1}),1.0]])]});}
            extrude(context, id + "F1", {"entities" : qUnion([Q0, Q1, Q2, Q3, Q4, Q5, Q6, Q7, Q8, Q9, Q10, Q11, Q12, Q13, Q14, Q15, Q16, Q17, Q18, Q19, Q20, Q21, Q22, Q23, Q24, Q25, Q26, Q27, Q28, Q29, Q30, Q31, Q32, Q33, Q34, Q35, Q36, Q37, Q38, Q39, Q40, Q41, Q42]), "depth" : 1.5 * mm});
        }
        {
            var Q0;
            Q0=makeQuery(id+"F1.opExtrude","SWEPT_BODY",BODY,{"disambiguationData":[OSD([sQuery(id+"F0.wireOp",EDGE,"E5"),sQuery(id+"F0.wireOp",EDGE,"E6"),sQuery(id+"F0.wireOp",EDGE,"E7"),sQuery(id+"F0.wireOp",EDGE,"E8"),sQuery(id+"F0.wireOp",EDGE,"E9"),sQuery(id+"F0.wireOp",EDGE,"E10"),sQuery(id+"F0.wireOp",EDGE,"E11"),sQuery(id+"F0.wireOp",EDGE,"E12"),sQuery(id+"F0.wireOp",EDGE,"E13"),sQuery(id+"F0.wireOp",EDGE,"E14"),sQuery(id+"F0.wireOp",EDGE,"E19"),sQuery(id+"F0.wireOp",EDGE,"E20"),sQuery(id+"F0.wireOp",EDGE,"E21"),sQuery(id+"F0.wireOp",EDGE,"E22"),sQuery(id+"F0.wireOp",EDGE,"E27.MirrorCS"),sQuery(id+"F0.wireOp",EDGE,"E29.MirrorCS"),sQuery(id+"F0.wireOp",EDGE,"E31.MirrorCS"),sQuery(id+"F0.wireOp",EDGE,"E33.MirrorCS"),sQuery(id+"F0.wireOp",EDGE,"E34.MirrorCS"),sQuery(id+"F0.wireOp",EDGE,"E35.MirrorCS"),sQuery(id+"F0.wireOp",EDGE,"E36.MirrorCS"),sQuery(id+"F0.wireOp",EDGE,"E37.MirrorCS"),sQuery(id+"F0.wireOp",EDGE,"E39.MirrorCS"),sQuery(id+"F0.wireOp",EDGE,"E43.MirrorCS"),sQuery(id+"F0.wireOp",EDGE,"E44.MirrorCS"),sQuery(id+"F0.wireOp",EDGE,"E45.MirrorCS"),sQuery(id+"F0.wireOp",EDGE,"E46.MirrorCS"),sQuery(id+"F0.wireOp",EDGE,"E48.MirrorCS"),sQuery(id+"F0.wireOp",EDGE,"E49.1.0"),sQuery(id+"F0.wireOp",EDGE,"E49.1.1"),sQuery(id+"F0.wireOp",EDGE,"E49.1.2"),sQuery(id+"F0.wireOp",EDGE,"E49.1.3"),sQuery(id+"F0.wireOp",EDGE,"E49.1.6"),sQuery(id+"F0.wireOp",EDGE,"E49.1.7"),sQuery(id+"F0.wireOp",EDGE,"E49.1.9"),sQuery(id+"F0.wireOp",EDGE,"E49.1.10"),sQuery(id+"F0.wireOp",EDGE,"E49.1.11"),sQuery(id+"F0.wireOp",EDGE,"E49.1.12"),sQuery(id+"F0.wireOp",EDGE,"E49.1.13"),sQuery(id+"F0.wireOp",EDGE,"E49.1.16"),sQuery(id+"F0.wireOp",EDGE,"E49.1.18"),sQuery(id+"F0.wireOp",EDGE,"E49.1.19"),sQuery(id+"F0.wireOp",EDGE,"E49.1.20"),sQuery(id+"F0.wireOp",EDGE,"E49.1.21"),sQuery(id+"F0.wireOp",EDGE,"E49.1.22"),sQuery(id+"F0.wireOp",EDGE,"E49.1.25"),sQuery(id+"F0.wireOp",EDGE,"E49.1.26"),sQuery(id+"F0.wireOp",EDGE,"E49.1.27"),sQuery(id+"F0.wireOp",EDGE,"E49.1.28"),sQuery(id+"F0.wireOp",EDGE,"E49.1.29"),sQuery(id+"F0.wireOp",EDGE,"E49.1.30"),sQuery(id+"F0.wireOp",EDGE,"E49.1.31"),sQuery(id+"F0.wireOp",EDGE,"E49.1.32"),sQuery(id+"F0.wireOp",EDGE,"E49.1.35"),sQuery(id+"F0.wireOp",EDGE,"E49.1.39"),sQuery(id+"F0.wireOp",EDGE,"E49.1.40"),sQuery(id+"F0.wireOp",EDGE,"E49.1.41"),sQuery(id+"F0.wireOp",EDGE,"E49.1.43"),sQuery(id+"F0.wireOp",EDGE,"E49.2.0"),sQuery(id+"F0.wireOp",EDGE,"E49.2.1"),sQuery(id+"F0.wireOp",EDGE,"E49.2.2"),sQuery(id+"F0.wireOp",EDGE,"E49.2.3"),sQuery(id+"F0.wireOp",EDGE,"E49.2.6"),sQuery(id+"F0.wireOp",EDGE,"E49.2.7"),sQuery(id+"F0.wireOp",EDGE,"E49.2.9"),sQuery(id+"F0.wireOp",EDGE,"E49.2.10"),sQuery(id+"F0.wireOp",EDGE,"E49.2.11"),sQuery(id+"F0.wireOp",EDGE,"E49.2.12"),sQuery(id+"F0.wireOp",EDGE,"E49.2.13"),sQuery(id+"F0.wireOp",EDGE,"E49.2.16"),sQuery(id+"F0.wireOp",EDGE,"E49.2.18"),sQuery(id+"F0.wireOp",EDGE,"E49.2.19"),sQuery(id+"F0.wireOp",EDGE,"E49.2.20"),sQuery(id+"F0.wireOp",EDGE,"E49.2.21"),sQuery(id+"F0.wireOp",EDGE,"E49.2.22"),sQuery(id+"F0.wireOp",EDGE,"E49.2.25"),sQuery(id+"F0.wireOp",EDGE,"E49.2.26"),sQuery(id+"F0.wireOp",EDGE,"E49.2.27"),sQuery(id+"F0.wireOp",EDGE,"E49.2.28"),sQuery(id+"F0.wireOp",EDGE,"E49.2.29"),sQuery(id+"F0.wireOp",EDGE,"E49.2.30"),sQuery(id+"F0.wireOp",EDGE,"E49.2.31"),sQuery(id+"F0.wireOp",EDGE,"E49.2.32"),sQuery(id+"F0.wireOp",EDGE,"E49.2.35"),sQuery(id+"F0.wireOp",EDGE,"E49.2.39"),sQuery(id+"F0.wireOp",EDGE,"E49.2.40"),sQuery(id+"F0.wireOp",EDGE,"E49.2.41"),sQuery(id+"F0.wireOp",EDGE,"E49.2.43"),sQuery(id+"F0.wireOp",EDGE,"E49.3.0"),sQuery(id+"F0.wireOp",EDGE,"E49.3.1"),sQuery(id+"F0.wireOp",EDGE,"E49.3.2"),sQuery(id+"F0.wireOp",EDGE,"E49.3.3"),sQuery(id+"F0.wireOp",EDGE,"E49.3.6"),sQuery(id+"F0.wireOp",EDGE,"E49.3.7"),sQuery(id+"F0.wireOp",EDGE,"E49.3.9"),sQuery(id+"F0.wireOp",EDGE,"E49.3.10"),sQuery(id+"F0.wireOp",EDGE,"E49.3.11"),sQuery(id+"F0.wireOp",EDGE,"E49.3.12"),sQuery(id+"F0.wireOp",EDGE,"E49.3.13"),sQuery(id+"F0.wireOp",EDGE,"E49.3.16"),sQuery(id+"F0.wireOp",EDGE,"E49.3.18"),sQuery(id+"F0.wireOp",EDGE,"E49.3.19"),sQuery(id+"F0.wireOp",EDGE,"E49.3.20"),sQuery(id+"F0.wireOp",EDGE,"E49.3.21"),sQuery(id+"F0.wireOp",EDGE,"E49.3.22"),sQuery(id+"F0.wireOp",EDGE,"E49.3.25"),sQuery(id+"F0.wireOp",EDGE,"E49.3.26"),sQuery(id+"F0.wireOp",EDGE,"E49.3.27"),sQuery(id+"F0.wireOp",EDGE,"E49.3.28"),sQuery(id+"F0.wireOp",EDGE,"E49.3.29"),sQuery(id+"F0.wireOp",EDGE,"E49.3.30"),sQuery(id+"F0.wireOp",EDGE,"E49.3.31"),sQuery(id+"F0.wireOp",EDGE,"E49.3.32"),sQuery(id+"F0.wireOp",EDGE,"E49.3.35"),sQuery(id+"F0.wireOp",EDGE,"E49.3.39"),sQuery(id+"F0.wireOp",EDGE,"E49.3.40"),sQuery(id+"F0.wireOp",EDGE,"E49.3.41"),sQuery(id+"F0.wireOp",EDGE,"E49.3.43"),sQuery(id+"F0.wireOp",EDGE,"E49.4.0"),sQuery(id+"F0.wireOp",EDGE,"E49.4.1"),sQuery(id+"F0.wireOp",EDGE,"E49.4.2"),sQuery(id+"F0.wireOp",EDGE,"E49.4.3"),sQuery(id+"F0.wireOp",EDGE,"E49.4.6"),sQuery(id+"F0.wireOp",EDGE,"E49.4.7"),sQuery(id+"F0.wireOp",EDGE,"E49.4.9"),sQuery(id+"F0.wireOp",EDGE,"E49.4.10"),sQuery(id+"F0.wireOp",EDGE,"E49.4.11"),sQuery(id+"F0.wireOp",EDGE,"E49.4.12"),sQuery(id+"F0.wireOp",EDGE,"E49.4.13"),sQuery(id+"F0.wireOp",EDGE,"E49.4.16"),sQuery(id+"F0.wireOp",EDGE,"E49.4.18"),sQuery(id+"F0.wireOp",EDGE,"E49.4.19"),sQuery(id+"F0.wireOp",EDGE,"E49.4.20"),sQuery(id+"F0.wireOp",EDGE,"E49.4.21"),sQuery(id+"F0.wireOp",EDGE,"E49.4.22"),sQuery(id+"F0.wireOp",EDGE,"E49.4.25"),sQuery(id+"F0.wireOp",EDGE,"E49.4.26"),sQuery(id+"F0.wireOp",EDGE,"E49.4.27"),sQuery(id+"F0.wireOp",EDGE,"E49.4.28"),sQuery(id+"F0.wireOp",EDGE,"E49.4.29"),sQuery(id+"F0.wireOp",EDGE,"E49.4.30"),sQuery(id+"F0.wireOp",EDGE,"E49.4.31"),sQuery(id+"F0.wireOp",EDGE,"E49.4.32"),sQuery(id+"F0.wireOp",EDGE,"E49.4.35"),sQuery(id+"F0.wireOp",EDGE,"E49.4.39"),sQuery(id+"F0.wireOp",EDGE,"E49.4.40"),sQuery(id+"F0.wireOp",EDGE,"E49.4.41"),sQuery(id+"F0.wireOp",EDGE,"E49.4.43"),sQuery(id+"F0.wireOp",EDGE,"E49.5.0"),sQuery(id+"F0.wireOp",EDGE,"E49.5.1"),sQuery(id+"F0.wireOp",EDGE,"E49.5.2"),sQuery(id+"F0.wireOp",EDGE,"E49.5.3"),sQuery(id+"F0.wireOp",EDGE,"E49.5.6"),sQuery(id+"F0.wireOp",EDGE,"E49.5.7"),sQuery(id+"F0.wireOp",EDGE,"E49.5.9"),sQuery(id+"F0.wireOp",EDGE,"E49.5.10"),sQuery(id+"F0.wireOp",EDGE,"E49.5.11"),sQuery(id+"F0.wireOp",EDGE,"E49.5.12"),sQuery(id+"F0.wireOp",EDGE,"E49.5.13"),sQuery(id+"F0.wireOp",EDGE,"E49.5.14"),sQuery(id+"F0.wireOp",EDGE,"E49.5.15"),sQuery(id+"F0.wireOp",EDGE,"E49.5.16"),sQuery(id+"F0.wireOp",EDGE,"E49.5.18"),sQuery(id+"F0.wireOp",EDGE,"E49.5.19"),sQuery(id+"F0.wireOp",EDGE,"E49.5.20"),sQuery(id+"F0.wireOp",EDGE,"E49.5.21"),sQuery(id+"F0.wireOp",EDGE,"E49.5.22"),sQuery(id+"F0.wireOp",EDGE,"E49.5.25"),sQuery(id+"F0.wireOp",EDGE,"E49.5.26"),sQuery(id+"F0.wireOp",EDGE,"E49.5.27"),sQuery(id+"F0.wireOp",EDGE,"E49.5.28"),sQuery(id+"F0.wireOp",EDGE,"E49.5.29"),sQuery(id+"F0.wireOp",EDGE,"E49.5.30"),sQuery(id+"F0.wireOp",EDGE,"E49.5.31"),sQuery(id+"F0.wireOp",EDGE,"E49.5.32"),sQuery(id+"F0.wireOp",EDGE,"E49.5.35"),sQuery(id+"F0.wireOp",EDGE,"E49.5.39"),sQuery(id+"F0.wireOp",EDGE,"E49.5.40"),sQuery(id+"F0.wireOp",EDGE,"E49.5.41"),sQuery(id+"F0.wireOp",EDGE,"E49.5.43")])]});
            var Q1;
            Q1=qCreatedBy(makeId("Origin.pointOp"),VERTEX);
            transform(context, id + "F2", {"entities" : qUnion([Q0]), "transformType" : TransformType.SCALE_UNIFORMLY, "scale" : 2, "scalePoint" : qUnion([Q1]), "makeCopy" : false});
        }
    });
